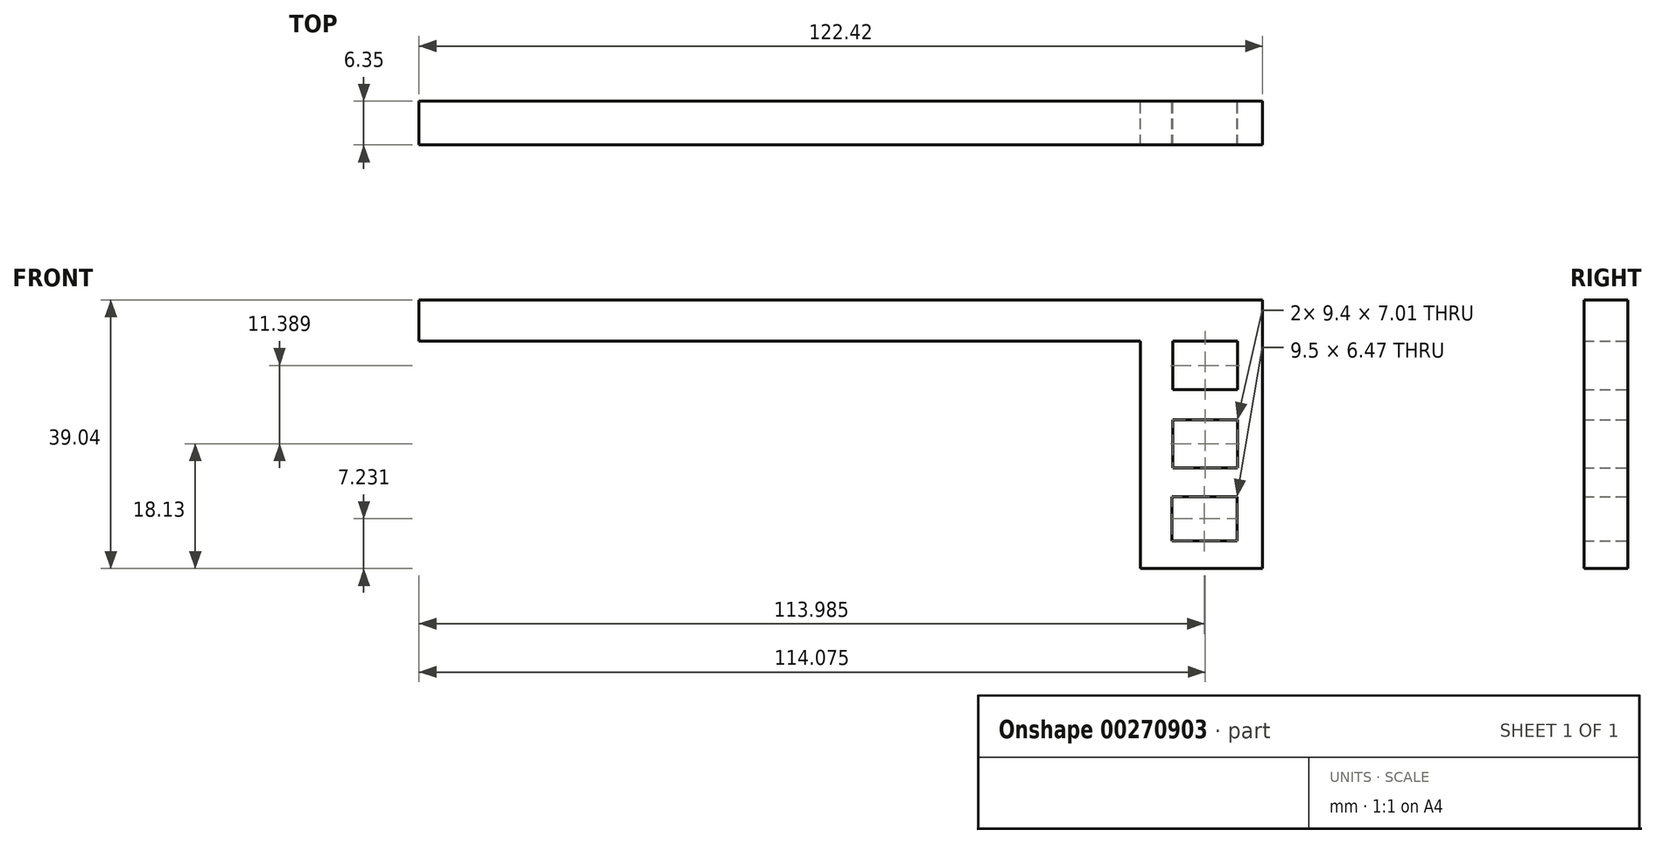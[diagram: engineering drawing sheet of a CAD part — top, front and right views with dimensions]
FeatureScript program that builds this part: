
annotation { "Feature Type Name" : "Feature", "Feature Type Description" : "" }
export const myFeature = defineFeature(function(context is Context, id is Id, definition is map)
    precondition{}
    {
        {
            var Q0;
            Q0=qCreatedBy(makeId("Front.planeOp"),FACE);
            var sketch = newSketch(context, id + "F1", { "sketchPlane" : qUnion([Q0])});
            skLineSegment(sketch, "E0", {"start": v(-60.46, 61.06) * mm, "end": v(61.96, 61.06) * mm});
            skLineSegment(sketch, "E1", {"start": v(44.22, 22.02) * mm, "end": v(44.22, 55.04) * mm});
            skLineSegment(sketch, "E2", {"start": v(61.96, 22.02) * mm, "end": v(61.96, 61.06) * mm});
            skLineSegment(sketch, "E3", {"start": v(-60.46, 61.06) * mm, "end": v(-60.46, 55.04) * mm});
            skLineSegment(sketch, "E4", {"start": v(-60.46, 55.04) * mm, "end": v(44.22, 55.04) * mm});
            skPoint(sketch, "E5.orphan", {"position": v(44.22, 61.06) * mm});
            skLineSegment(sketch, "E6.bottom", {"start": v(48.91, 48.03) * mm, "end": v(58.32, 48.03) * mm});
            skLineSegment(sketch, "E6.top", {"start": v(48.91, 55.04) * mm, "end": v(58.32, 55.04) * mm});
            skLineSegment(sketch, "E6.left", {"start": v(48.91, 48.03) * mm, "end": v(48.91, 55.04) * mm});
            skLineSegment(sketch, "E6.right", {"start": v(58.32, 48.03) * mm, "end": v(58.32, 55.04) * mm});
            skLineSegment(sketch, "E7.bottom", {"start": v(48.91, 43.66) * mm, "end": v(58.32, 43.66) * mm});
            skLineSegment(sketch, "E7.top", {"start": v(48.91, 36.64) * mm, "end": v(58.32, 36.64) * mm});
            skLineSegment(sketch, "E7.left", {"start": v(48.91, 43.66) * mm, "end": v(48.91, 36.64) * mm});
            skLineSegment(sketch, "E7.right", {"start": v(58.32, 43.66) * mm, "end": v(58.32, 36.64) * mm});
            skLineSegment(sketch, "E8.bottom", {"start": v(48.78, 32.49) * mm, "end": v(58.27, 32.49) * mm});
            skLineSegment(sketch, "E8.top", {"start": v(48.78, 26.01) * mm, "end": v(58.27, 26.01) * mm});
            skLineSegment(sketch, "E8.left", {"start": v(48.78, 32.49) * mm, "end": v(48.78, 26.01) * mm});
            skLineSegment(sketch, "E8.right", {"start": v(58.27, 32.49) * mm, "end": v(58.27, 26.01) * mm});
            skLineSegment(sketch, "E9", {"start": v(44.22, 22.02) * mm, "end": v(61.96, 22.02) * mm});
            skPoint(sketch, "E10.orphan", {"position": v(44.22, 31.28) * mm});
            skPoint(sketch, "E11.orphan", {"position": v(61.96, 31.28) * mm});
            skSolve(sketch);
        }
        {
            var Q0;
            Q0 = qSketchRegion(id + "F1", true);
            extrude(context, id + "F0", {"entities" : qUnion([Q0]), "depth" : 6.35 * mm});
        }
    });
